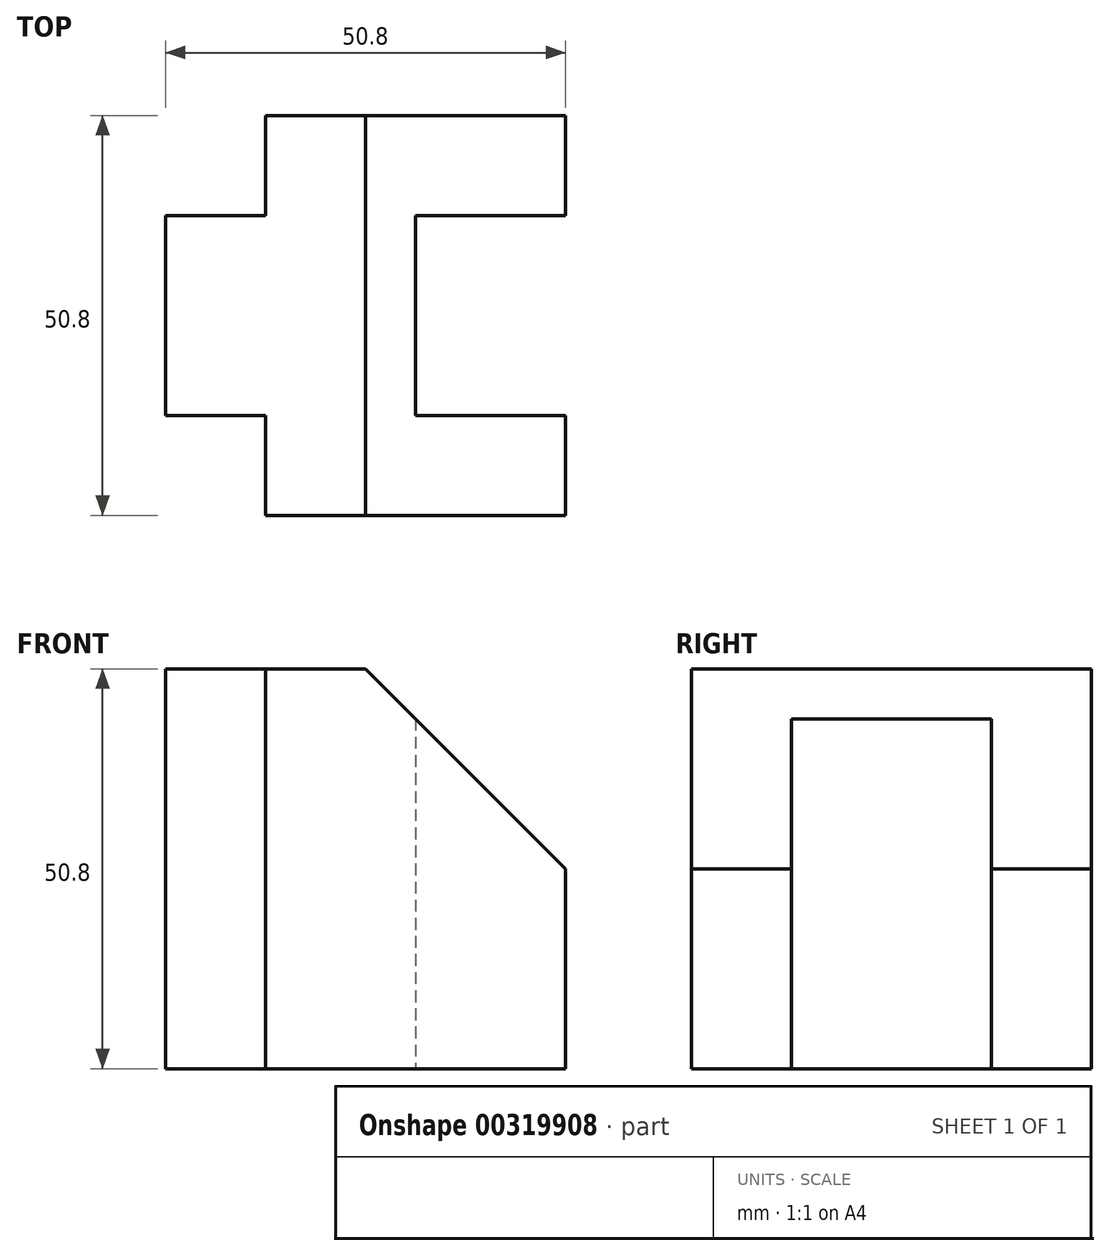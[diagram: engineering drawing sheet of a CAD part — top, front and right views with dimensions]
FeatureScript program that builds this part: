
annotation { "Feature Type Name" : "Feature", "Feature Type Description" : "" }
export const myFeature = defineFeature(function(context is Context, id is Id, definition is map)
    precondition{}
    {
        {
            var Q0;
            Q0=qCreatedBy(makeId("Top.planeOp"),FACE);
            var sketch = newSketch(context, id + "F0", { "sketchPlane" : qUnion([Q0])});
            skLineSegment(sketch, "E0", {"start": v(25.4, 0) * mm, "end": v(25.4, 12.7) * mm});
            skLineSegment(sketch, "E1", {"start": v(25.4, 12.7) * mm, "end": v(6.35, 12.7) * mm});
            skLineSegment(sketch, "E2", {"start": v(6.35, 12.7) * mm, "end": v(6.35, 38.1) * mm});
            skLineSegment(sketch, "E3", {"start": v(6.35, 38.1) * mm, "end": v(25.4, 38.1) * mm});
            skLineSegment(sketch, "E4", {"start": v(25.4, 38.1) * mm, "end": v(25.4, 50.8) * mm});
            skLineSegment(sketch, "E5", {"start": v(25.4, 0) * mm, "end": v(-12.7, 0) * mm});
            skLineSegment(sketch, "E6", {"start": v(-12.7, 0) * mm, "end": v(-12.7, 12.7) * mm});
            skLineSegment(sketch, "E7", {"start": v(-12.7, 12.7) * mm, "end": v(-25.4, 12.7) * mm});
            skLineSegment(sketch, "E8", {"start": v(-25.4, 12.7) * mm, "end": v(-25.4, 38.1) * mm});
            skLineSegment(sketch, "E9", {"start": v(-25.4, 38.1) * mm, "end": v(-12.7, 38.1) * mm});
            skLineSegment(sketch, "E10", {"start": v(-12.7, 38.1) * mm, "end": v(-12.7, 50.8) * mm});
            skLineSegment(sketch, "E11", {"start": v(-12.7, 50.8) * mm, "end": v(25.4, 50.8) * mm});
            skSolve(sketch);
        }
        {
            var Q0;
            Q0 = qSketchRegion(id + "F0", true);
            extrude(context, id + "F1", {"entities" : qUnion([Q0]), "depth" : 50.8 * mm});
        }
        {
            var Q0;
            Q0=qCreatedBy(makeId("Front.planeOp"),FACE);
            var sketch = newSketch(context, id + "F2", { "sketchPlane" : qUnion([Q0])});
            skLineSegment(sketch, "E12", {"start": v(0, 50.8) * mm, "end": v(25.4, 25.4) * mm});
            skLineSegment(sketch, "E13", {"start": v(25.4, 25.4) * mm, "end": v(25.4, 50.8) * mm});
            skLineSegment(sketch, "E14", {"start": v(0, 50.8) * mm, "end": v(25.4, 50.8) * mm});
            skSolve(sketch);
        }
        {
            var Q0;
            Q0 = qSketchRegion(id + "F2", true);
            extrude(context, id + "F3", {"entities" : qUnion([Q0]), "operationType" : NewBodyOperationType.REMOVE, "endBound" : BoundingType.THROUGH_ALL, "oppositeDirection" : true, "depth" : 25.4 * mm});
        }
    });
